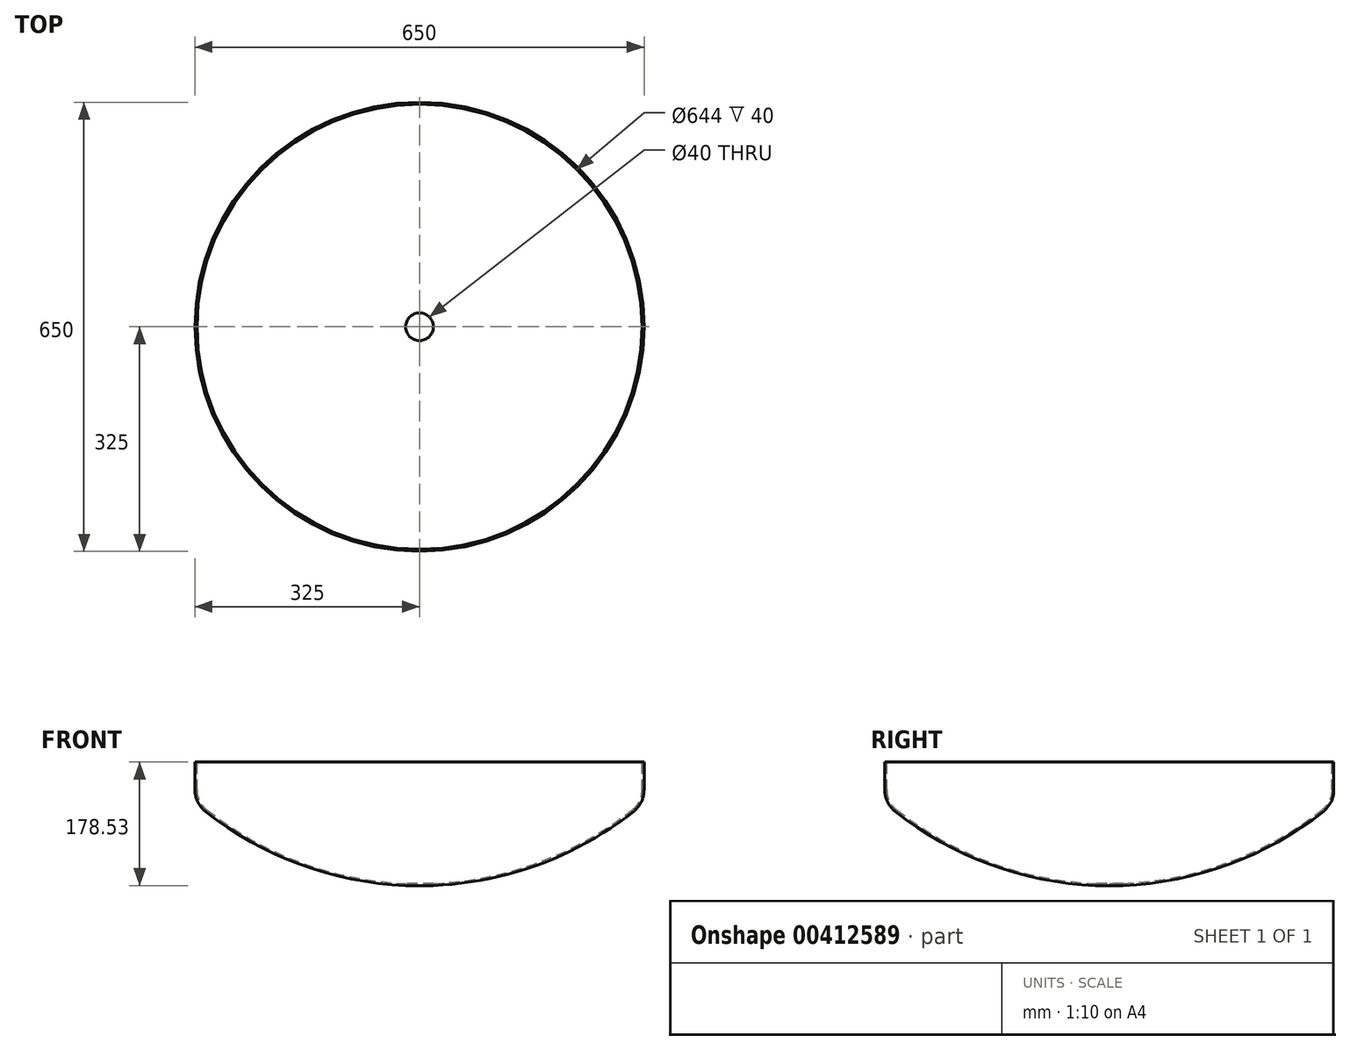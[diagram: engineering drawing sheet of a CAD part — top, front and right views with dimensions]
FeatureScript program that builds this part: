
annotation { "Feature Type Name" : "Feature", "Feature Type Description" : "" }
export const myFeature = defineFeature(function(context is Context, id is Id, definition is map)
    precondition{}
    {
        {
            var Q0;
            Q0=qCreatedBy(makeId("Front.planeOp"),FACE);
            var sketch = newSketch(context, id + "F0", { "sketchPlane" : qUnion([Q0])});
            skLineSegment(sketch, "E0", {"start": v(325, 0) * mm, "end": v(325, -40) * mm});
            skArc(sketch, "E1", {"start": v(325, -40) * mm, "mid": v(321, -57.45) * mm, "end": v(309.78, -71.4) * mm});
            skArc(sketch, "E2", {"start": v(309.78, -71.4) * mm, "mid": v(173.37, -147.9) * mm, "end": v(20, -178.53) * mm});
            skLineSegment(sketch, "E3", {"start": v(325, 0) * mm, "end": v(322, 0) * mm});
            skLineSegment(sketch, "E4", {"start": v(322, 0) * mm, "end": v(322, -40) * mm});
            skArc(sketch, "E5", {"start": v(322, -40) * mm, "mid": v(318.28, -56.17) * mm, "end": v(307.87, -69.09) * mm});
            skArc(sketch, "E6", {"start": v(307.87, -69.09) * mm, "mid": v(172.36, -145.08) * mm, "end": v(20, -175.52) * mm});
            skLineSegment(sketch, "E7", {"start": v(20, -175.52) * mm, "end": v(20, -178.53) * mm});
            skSolve(sketch);
        }
        {
            var Q0;
            Q0=qCreatedBy(makeId("Front.planeOp"),FACE);
            var sketch = newSketch(context, id + "F1", { "sketchPlane" : qUnion([Q0])});
            skLineSegment(sketch, "E8", {"start": v(0, 0) * mm, "end": v(0, -195.76) * mm, "construction": true});
            skSolve(sketch);
        }
        {
            var Q0;
            Q0 = qSketchRegion(id + "F0", true);
            var Q1;
            Q1=sQuery(id+"F1.wireOp",EDGE,"E8");
            revolve(context, id + "F2", {"entities" : qUnion([Q0]), "axis" : qUnion([Q1]), "revolveType" : RevolveType.FULL});
        }
    });
